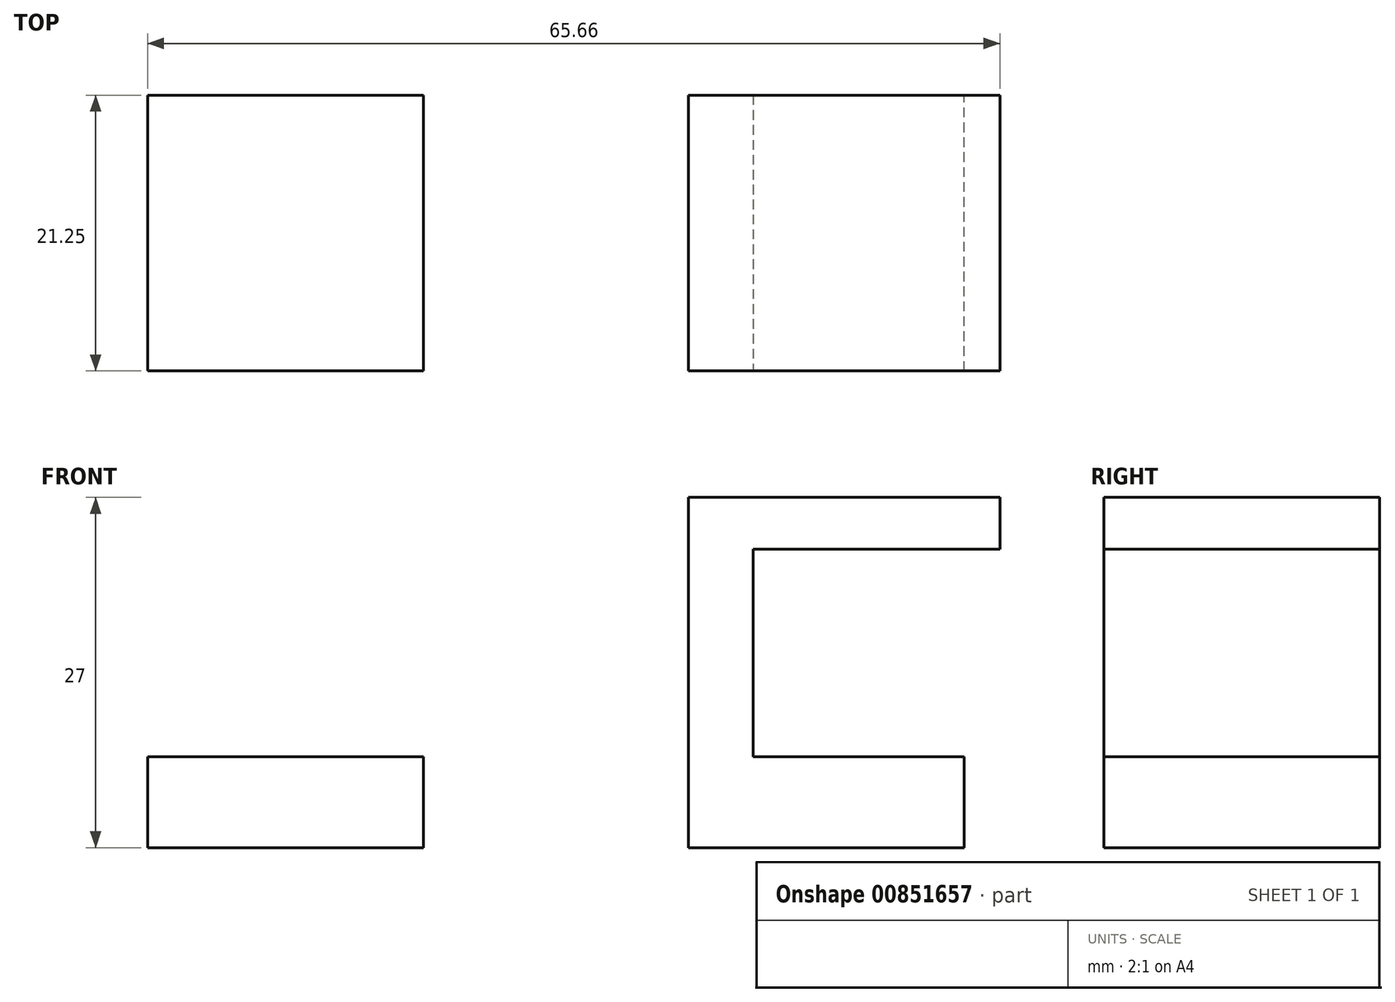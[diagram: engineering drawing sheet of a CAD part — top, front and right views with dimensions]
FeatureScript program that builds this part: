
annotation { "Feature Type Name" : "Feature", "Feature Type Description" : "" }
export const myFeature = defineFeature(function(context is Context, id is Id, definition is map)
    precondition{}
    {
        {
            var Q0;
            Q0=qCreatedBy(makeId("Front.planeOp"),FACE);
            var sketch = newSketch(context, id + "F0", { "sketchPlane" : qUnion([Q0])});
            skLineSegment(sketch, "E0.bottom", {"start": v(0, 0) * mm, "end": v(21.25, 0) * mm});
            skLineSegment(sketch, "E1", {"start": v(0, 0) * mm, "end": v(0, 7) * mm});
            skLineSegment(sketch, "E2", {"start": v(0, 7) * mm, "end": v(21.25, 7) * mm});
            skLineSegment(sketch, "E3", {"start": v(21.25, 7) * mm, "end": v(21.25, 0) * mm});
            skSolve(sketch);
        }
        {
            var Q0;
            Q0=makeQuery(id+"F0.imprint","IMPRINT",FACE,{"disambiguationData":[TD([[makeQuery(id+"F0.imprint","IMPRINT",EDGE,{"derivedFrom":sQuery(id+"F0.wireOp",EDGE,"E0.bottom")}),1.0]])]});
            extrude(context, id + "F1", {"entities" : qUnion([Q0]), "depth" : 21.25 * mm, "offsetDistance" : 25 * mm});
        }
        {
            var Q0;
            Q0=makeQuery(id+"F1.opExtrude","SWEPT_FACE",FACE,{"disambiguationData":[OSD([sQuery(id+"F0.wireOp",EDGE,"E2")])]});
            var sketch = newSketch(context, id + "F2", { "sketchPlane" : qUnion([Q0])});
            skLineSegment(sketch, "E4.bottom", {"start": v(0, 0) * mm, "end": v(5, 0) * mm});
            skLineSegment(sketch, "E4.top", {"start": v(0, -21.25) * mm, "end": v(5, -21.25) * mm});
            skLineSegment(sketch, "E4.left", {"start": v(0, 0) * mm, "end": v(0, -21.25) * mm});
            skLineSegment(sketch, "E4.right", {"start": v(5, 0) * mm, "end": v(5, -21.25) * mm});
            skSolve(sketch);
        }
        {
            var Q0;
            Q0=makeQuery(id+"F2.imprint","IMPRINT",FACE,{"disambiguationData":[TD([[makeQuery(id+"F2.imprint","IMPRINT",EDGE,{"derivedFrom":sQuery(id+"F2.wireOp",EDGE,"E4.bottom")}),-1.0]])]});
            extrude(context, id + "F3", {"entities" : qUnion([Q0]), "operationType" : NewBodyOperationType.ADD, "depth" : 20 * mm, "offsetDistance" : 25 * mm});
        }
        {
            var Q0;
            Q0=makeQuery(id+"F3.opExtrude","CAP_FACE",FACE,{"disambiguationData":[OSD([sQuery(id+"F2.wireOp",EDGE,"E4.bottom"),sQuery(id+"F2.wireOp",EDGE,"E4.top"),sQuery(id+"F2.wireOp",EDGE,"E4.left"),sQuery(id+"F2.wireOp",EDGE,"E4.right")])],"isStart":false});
            var sketch = newSketch(context, id + "F4", { "sketchPlane" : qUnion([Q0])});
            skLineSegment(sketch, "E5.bottom", {"start": v(0, -21.25) * mm, "end": v(24, -21.25) * mm});
            skLineSegment(sketch, "E5.top", {"start": v(0, 0) * mm, "end": v(24, 0) * mm});
            skLineSegment(sketch, "E5.left", {"start": v(0, -21.25) * mm, "end": v(0, 0) * mm});
            skLineSegment(sketch, "E5.right", {"start": v(24, -21.25) * mm, "end": v(24, 0) * mm});
            skSolve(sketch);
        }
        {
            var Q0;
            {var subQ2=sQuery(id+"F4.wireOp",EDGE,"E5.right");Q0=makeQuery(id+"F4.imprint","IMPRINT",FACE,{"disambiguationData":[TD([[makeQuery(id+"F4.imprint","IMPRINT",EDGE,{"derivedFrom":subQ2}),1.0]])]});}
            extrude(context, id + "F5", {"entities" : qUnion([Q0]), "operationType" : NewBodyOperationType.ADD, "oppositeDirection" : true, "depth" : 4 * mm, "offsetDistance" : 25 * mm});
        }
        {
            var Q0;
            Q0=qCreatedBy(makeId("Front.planeOp"),FACE);
            var sketch = newSketch(context, id + "F6", { "sketchPlane" : qUnion([Q0])});
            skLineSegment(sketch, "E6.bottom", {"start": v(-41.66, 0) * mm, "end": v(-20.4, 0) * mm});
            skLineSegment(sketch, "E6.top", {"start": v(-41.66, 7) * mm, "end": v(-20.4, 7) * mm});
            skLineSegment(sketch, "E6.left", {"start": v(-41.66, 0) * mm, "end": v(-41.66, 7) * mm});
            skLineSegment(sketch, "E6.right", {"start": v(-20.4, 0) * mm, "end": v(-20.4, 7) * mm});
            skSolve(sketch);
        }
        {
            var Q0;
            Q0=makeQuery(id+"F6.imprint","IMPRINT",FACE,{"disambiguationData":[TD([[makeQuery(id+"F6.imprint","IMPRINT",EDGE,{"derivedFrom":sQuery(id+"F6.wireOp",EDGE,"E6.bottom")}),1.0]])]});
            extrude(context, id + "F7", {"entities" : qUnion([Q0]), "depth" : 21.25 * mm, "offsetDistance" : 25 * mm});
        }
    });
